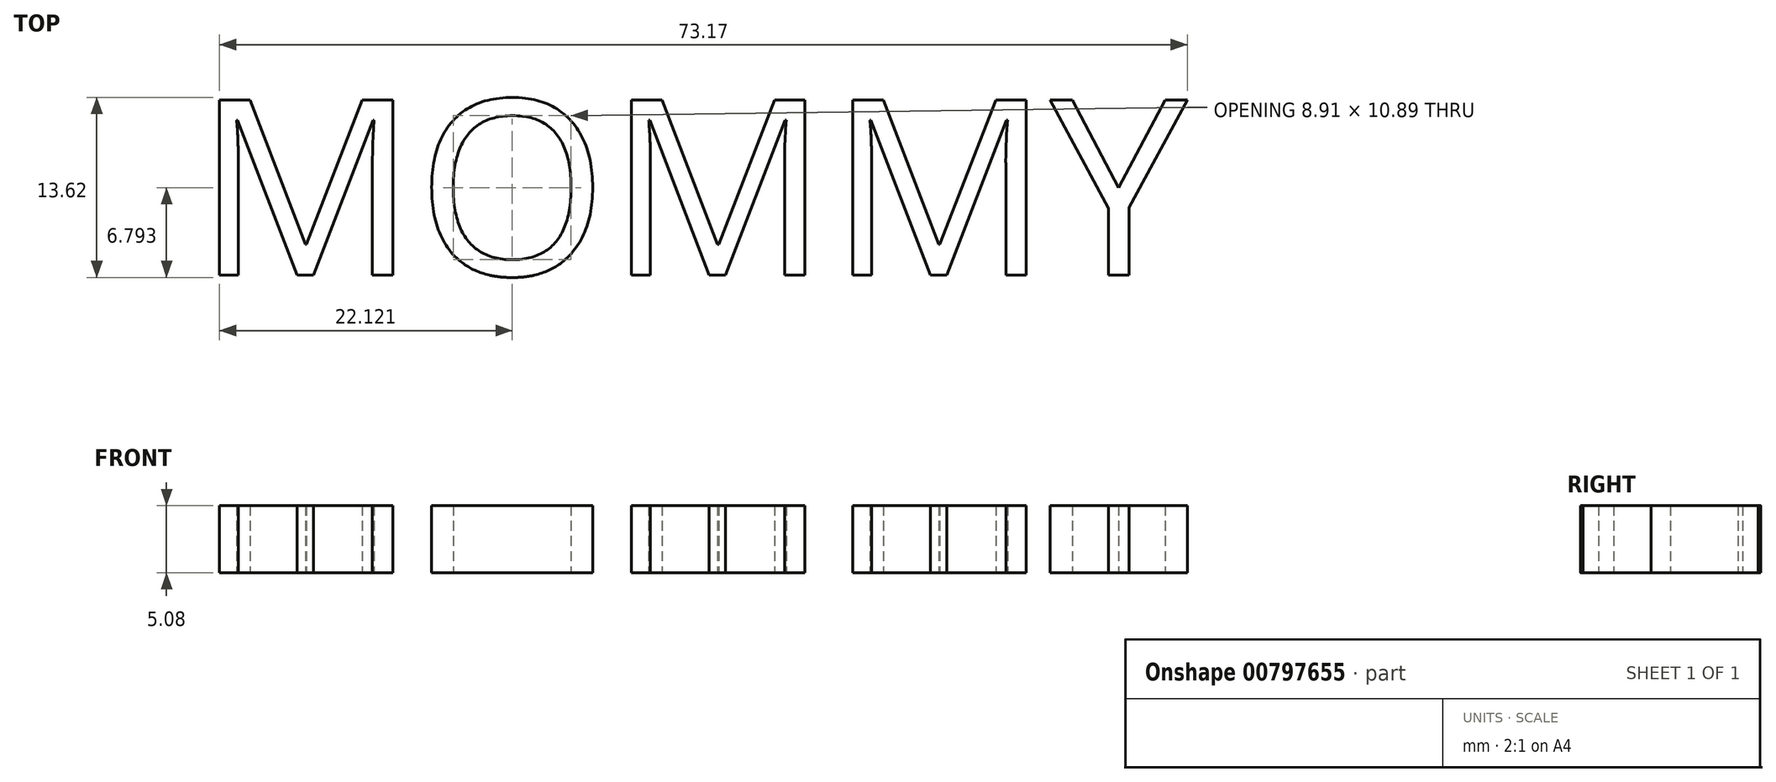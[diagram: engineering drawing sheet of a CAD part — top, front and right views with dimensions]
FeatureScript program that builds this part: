
annotation { "Feature Type Name" : "Feature", "Feature Type Description" : "" }
export const myFeature = defineFeature(function(context is Context, id is Id, definition is map)
    precondition{}
    {
        {
            var Q0;
            Q0=qCreatedBy(makeId("Top.planeOp"),FACE);
            var sketch = newSketch(context, id + "F0", { "sketchPlane" : qUnion([Q0])});
            skText(sketch, "E0", { "text": "MOMMY", "fontName": "OpenSans-Regular.ttf"});
            skPoint(sketch, "E1", {"position": v(0, 0) * mm});
            skLineSegment(sketch, "E2.bottom", {"start": v(-47, -6.67) * mm, "end": v(47, -6.67) * mm});
            skLineSegment(sketch, "E2.top", {"start": v(-47, -6.67) * mm, "end": v(47, -6.67) * mm});
            skLineSegment(sketch, "E2.left", {"start": v(-47, -6.67) * mm, "end": v(-47, -6.67) * mm});
            skLineSegment(sketch, "E2.right", {"start": v(47, -6.67) * mm, "end": v(47, -6.67) * mm});
            skPoint(sketch, "E2.middle", {"position": v(0, -6.67) * mm});
            skLineSegment(sketch, "E3.top", {"start": v(-47, -11.75) * mm, "end": v(47, -11.75) * mm});
            skLineSegment(sketch, "E3.left", {"start": v(-47, -6.67) * mm, "end": v(-47, -11.75) * mm});
            skLineSegment(sketch, "E3.right", {"start": v(47, -6.67) * mm, "end": v(47, -11.75) * mm});
            const initialGuessF0  = {"E0": [-0.0381, -0.00667, 1, 0, 0.01334]};
            skSetInitialGuess(sketch, initialGuessF0);
            skSolve(sketch);
        }
        {
            var Q0;
            {var subQ16=sQuery(id+"F0.wireOp",EDGE,"E0.sketch_text.stroke-20");var subQ19=sQuery(id+"F0.wireOp",EDGE,"E0.sketch_text.stroke-19");var subQ22=sQuery(id+"F0.wireOp",EDGE,"E0.sketch_text.stroke-4");var subQ26=makeQuery(id+"F0.imprint","IMPRINT",EDGE,{"derivedFrom":subQ22});var subQ30=sQuery(id+"F0.wireOp",EDGE,"E0.sketch_text.stroke-0");var subQ32=makeQuery(id+"F0.imprint","INTERSECT",VERTEX,{"derivedFrom":[subQ19,subQ16]});var subQ42=sQuery(id+"F0.wireOp",EDGE,"E0.sketch_text.stroke-52");var subQ44=makeQuery(id+"F0.imprint","IMPRINT",EDGE,{"disambiguationData":[TD([[subQ32,1.0]])],"derivedFrom":subQ19});var subQ46=sQuery(id+"F0.wireOp",EDGE,"E0.sketch_text.stroke-34");var subQ51=sQuery(id+"F0.wireOp",EDGE,"E0.sketch_text.stroke-18");Q0=qUnion([makeQuery(id+"F0.imprint","IMPRINT",FACE,{"disambiguationData":[TD([[makeQuery(id+"F0.imprint","IMPRINT",EDGE,{"derivedFrom":sQuery(id+"F0.wireOp",EDGE,"E0.sketch_text.stroke-70")}),-1.0]])]}),makeQuery(id+"F0.imprint","IMPRINT",FACE,{"disambiguationData":[TD([[makeQuery(id+"F0.imprint","IMPRINT",EDGE,{"derivedFrom":subQ51}),-1.0]])]}),makeQuery(id+"F0.imprint","IMPRINT",FACE,{"disambiguationData":[TD([[subQ44,-1.0]])]}),makeQuery(id+"F0.imprint","IMPRINT",FACE,{"disambiguationData":[TD([[makeQuery(id+"F0.imprint","IMPRINT",EDGE,{"derivedFrom":subQ30}),-1.0]])]}),makeQuery(id+"F0.imprint","IMPRINT",FACE,{"disambiguationData":[TD([[makeQuery(id+"F0.imprint","IMPRINT",EDGE,{"derivedFrom":subQ46}),-1.0]])]}),makeQuery(id+"F0.imprint","IMPRINT",FACE,{"disambiguationData":[TD([[makeQuery(id+"F0.imprint","IMPRINT",EDGE,{"derivedFrom":subQ42}),-1.0]])]}),makeQuery(id+"F0.imprint","IMPRINT",FACE,{"disambiguationData":[TD([[subQ26,1.0]])]})]);}
            extrude(context, id + "F1", {"entities" : qUnion([Q0]), "depth" : 5.08 * mm, "offsetDistance" : 25.4 * mm});
        }
        {
            var Q0;
            Q0=makeQuery(id+"F1.opExtrude","CAP_FACE",FACE,{"disambiguationData":[OSD([sQuery(id+"F0.wireOp",EDGE,"E0.sketch_text.stroke-0"),sQuery(id+"F0.wireOp",EDGE,"E0.sketch_text.stroke-1"),sQuery(id+"F0.wireOp",EDGE,"E0.sketch_text.stroke-2"),sQuery(id+"F0.wireOp",EDGE,"E0.sketch_text.stroke-3"),sQuery(id+"F0.wireOp",EDGE,"E0.sketch_text.stroke-5"),sQuery(id+"F0.wireOp",EDGE,"E0.sketch_text.stroke-6"),sQuery(id+"F0.wireOp",EDGE,"E0.sketch_text.stroke-7"),sQuery(id+"F0.wireOp",EDGE,"E0.sketch_text.stroke-8"),sQuery(id+"F0.wireOp",EDGE,"E0.sketch_text.stroke-9"),sQuery(id+"F0.wireOp",EDGE,"E0.sketch_text.stroke-10"),sQuery(id+"F0.wireOp",EDGE,"E0.sketch_text.stroke-11"),sQuery(id+"F0.wireOp",EDGE,"E0.sketch_text.stroke-13"),sQuery(id+"F0.wireOp",EDGE,"E0.sketch_text.stroke-14"),sQuery(id+"F0.wireOp",EDGE,"E0.sketch_text.stroke-15"),sQuery(id+"F0.wireOp",EDGE,"E0.sketch_text.stroke-16"),sQuery(id+"F0.wireOp",EDGE,"E0.sketch_text.stroke-18"),sQuery(id+"F0.wireOp",EDGE,"E0.sketch_text.stroke-19"),sQuery(id+"F0.wireOp",EDGE,"E0.sketch_text.stroke-20"),sQuery(id+"F0.wireOp",EDGE,"E0.sketch_text.stroke-21"),sQuery(id+"F0.wireOp",EDGE,"E0.sketch_text.stroke-22"),sQuery(id+"F0.wireOp",EDGE,"E0.sketch_text.stroke-23"),sQuery(id+"F0.wireOp",EDGE,"E0.sketch_text.stroke-24"),sQuery(id+"F0.wireOp",EDGE,"E0.sketch_text.stroke-25"),sQuery(id+"F0.wireOp",EDGE,"E0.sketch_text.stroke-26"),sQuery(id+"F0.wireOp",EDGE,"E0.sketch_text.stroke-27"),sQuery(id+"F0.wireOp",EDGE,"E0.sketch_text.stroke-28"),sQuery(id+"F0.wireOp",EDGE,"E0.sketch_text.stroke-29"),sQuery(id+"F0.wireOp",EDGE,"E0.sketch_text.stroke-30"),sQuery(id+"F0.wireOp",EDGE,"E0.sketch_text.stroke-31"),sQuery(id+"F0.wireOp",EDGE,"E0.sketch_text.stroke-32"),sQuery(id+"F0.wireOp",EDGE,"E0.sketch_text.stroke-33"),sQuery(id+"F0.wireOp",EDGE,"E0.sketch_text.stroke-34"),sQuery(id+"F0.wireOp",EDGE,"E0.sketch_text.stroke-35"),sQuery(id+"F0.wireOp",EDGE,"E0.sketch_text.stroke-36"),sQuery(id+"F0.wireOp",EDGE,"E0.sketch_text.stroke-37"),sQuery(id+"F0.wireOp",EDGE,"E0.sketch_text.stroke-39"),sQuery(id+"F0.wireOp",EDGE,"E0.sketch_text.stroke-40"),sQuery(id+"F0.wireOp",EDGE,"E0.sketch_text.stroke-41"),sQuery(id+"F0.wireOp",EDGE,"E0.sketch_text.stroke-42"),sQuery(id+"F0.wireOp",EDGE,"E0.sketch_text.stroke-43"),sQuery(id+"F0.wireOp",EDGE,"E0.sketch_text.stroke-44"),sQuery(id+"F0.wireOp",EDGE,"E0.sketch_text.stroke-45"),sQuery(id+"F0.wireOp",EDGE,"E0.sketch_text.stroke-47"),sQuery(id+"F0.wireOp",EDGE,"E0.sketch_text.stroke-48"),sQuery(id+"F0.wireOp",EDGE,"E0.sketch_text.stroke-49"),sQuery(id+"F0.wireOp",EDGE,"E0.sketch_text.stroke-50"),sQuery(id+"F0.wireOp",EDGE,"E0.sketch_text.stroke-52"),sQuery(id+"F0.wireOp",EDGE,"E0.sketch_text.stroke-53"),sQuery(id+"F0.wireOp",EDGE,"E0.sketch_text.stroke-54"),sQuery(id+"F0.wireOp",EDGE,"E0.sketch_text.stroke-55"),sQuery(id+"F0.wireOp",EDGE,"E0.sketch_text.stroke-57"),sQuery(id+"F0.wireOp",EDGE,"E0.sketch_text.stroke-58"),sQuery(id+"F0.wireOp",EDGE,"E0.sketch_text.stroke-59"),sQuery(id+"F0.wireOp",EDGE,"E0.sketch_text.stroke-60"),sQuery(id+"F0.wireOp",EDGE,"E0.sketch_text.stroke-61"),sQuery(id+"F0.wireOp",EDGE,"E0.sketch_text.stroke-62"),sQuery(id+"F0.wireOp",EDGE,"E0.sketch_text.stroke-63"),sQuery(id+"F0.wireOp",EDGE,"E0.sketch_text.stroke-65"),sQuery(id+"F0.wireOp",EDGE,"E0.sketch_text.stroke-66"),sQuery(id+"F0.wireOp",EDGE,"E0.sketch_text.stroke-67"),sQuery(id+"F0.wireOp",EDGE,"E0.sketch_text.stroke-68"),sQuery(id+"F0.wireOp",EDGE,"E0.sketch_text.stroke-70"),sQuery(id+"F0.wireOp",EDGE,"E0.sketch_text.stroke-71"),sQuery(id+"F0.wireOp",EDGE,"E0.sketch_text.stroke-72"),sQuery(id+"F0.wireOp",EDGE,"E0.sketch_text.stroke-73"),sQuery(id+"F0.wireOp",EDGE,"E0.sketch_text.stroke-75"),sQuery(id+"F0.wireOp",EDGE,"E0.sketch_text.stroke-76"),sQuery(id+"F0.wireOp",EDGE,"E0.sketch_text.stroke-77"),sQuery(id+"F0.wireOp",EDGE,"E0.sketch_text.stroke-78"),sQuery(id+"F0.wireOp",EDGE,"E2.bottom"),sQuery(id+"F0.wireOp",EDGE,"E3.top"),sQuery(id+"F0.wireOp",EDGE,"E3.left"),sQuery(id+"F0.wireOp",EDGE,"E3.right")])],"isStart":false});
            var sketch = newSketch(context, id + "F2", { "sketchPlane" : qUnion([Q0])});
            skText(sketch, "E4", { "text": "We Love You!", "fontName": "RobotoSlab-Regular.ttf"});
            skPoint(sketch, "E5", {"position": v(-44.45, -9.21) * mm});
            skLineSegment(sketch, "E6.bottom", {"start": v(-47, -6.67) * mm, "end": v(-44.45, -6.67) * mm, "construction": true});
            skLineSegment(sketch, "E6.top", {"start": v(-47, -11.75) * mm, "end": v(-44.45, -11.75) * mm, "construction": true});
            skLineSegment(sketch, "E6.left", {"start": v(-47, -6.67) * mm, "end": v(-47, -11.75) * mm, "construction": true});
            skLineSegment(sketch, "E6.right", {"start": v(-44.45, -6.67) * mm, "end": v(-44.45, -11.75) * mm, "construction": true});
            const initialGuessF2  = {"E4": [-0.04445, -0.01112, 1, 0, 0.00381]};
            skSetInitialGuess(sketch, initialGuessF2);
            skSolve(sketch);
        }
        {
            var Q0;
            Q0 = qSketchRegion(id + "F2", true);
            extrude(context, id + "F3", {"entities" : qUnion([Q0]), "operationType" : NewBodyOperationType.REMOVE, "oppositeDirection" : true, "depth" : 1.27 * mm, "offsetDistance" : 25.4 * mm});
        }
    });
